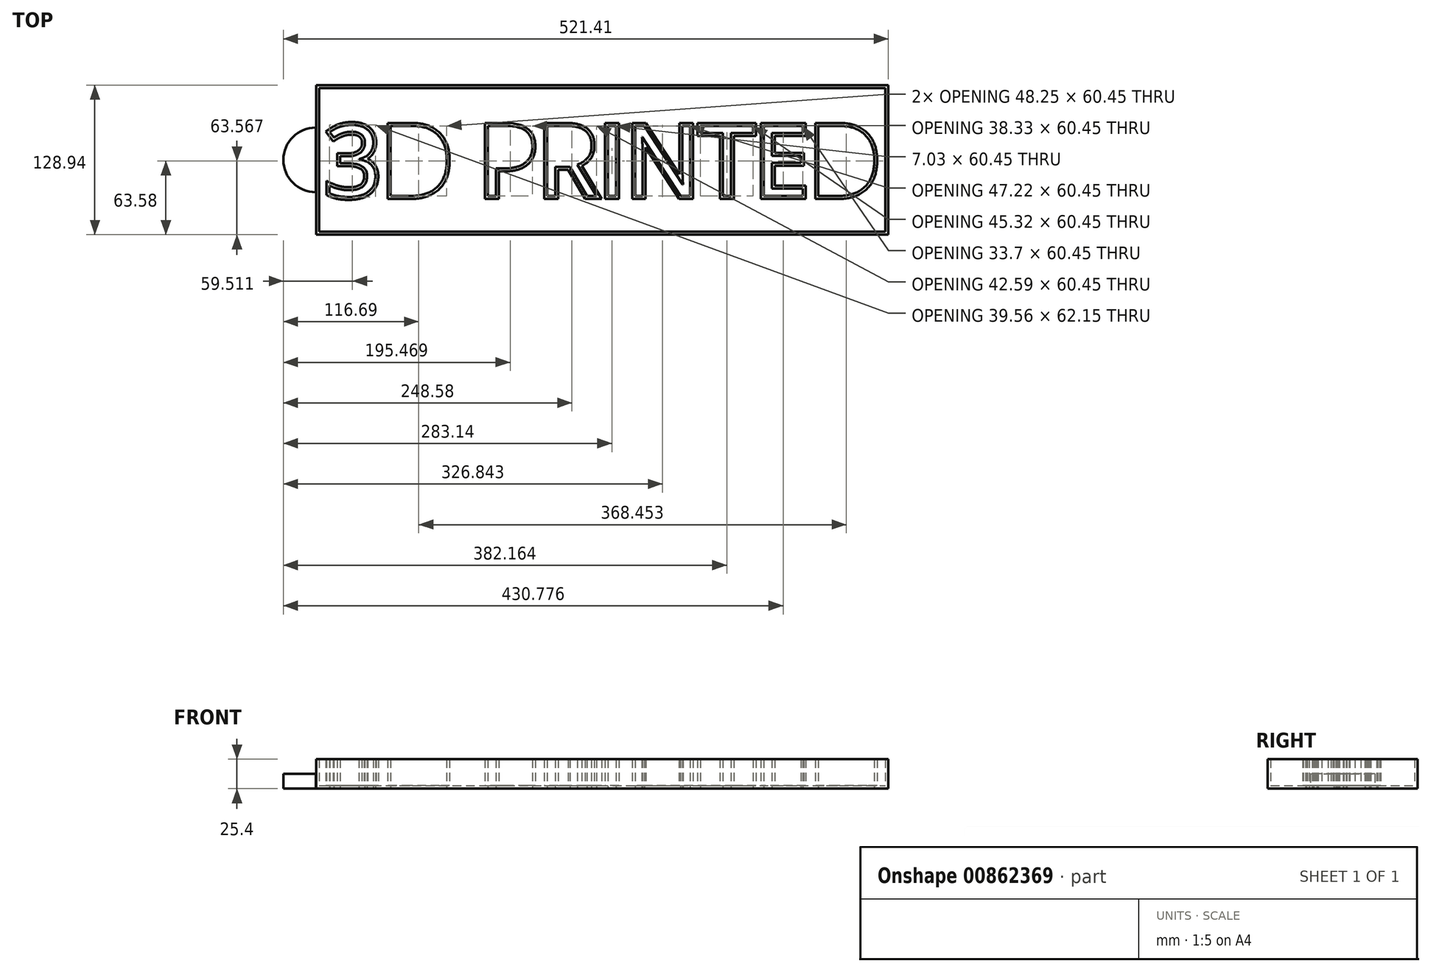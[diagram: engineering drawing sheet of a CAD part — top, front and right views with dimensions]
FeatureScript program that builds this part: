
annotation { "Feature Type Name" : "Feature", "Feature Type Description" : "" }
export const myFeature = defineFeature(function(context is Context, id is Id, definition is map)
    precondition{}
    {
        {
            var Q0;
            Q0=qCreatedBy(makeId("Top.planeOp"),FACE);
            var sketch = newSketch(context, id + "F0", { "sketchPlane" : qUnion([Q0])});
            skLineSegment(sketch, "E0.bottom", {"start": v(-246.53, -64.47) * mm, "end": v(246.53, -64.47) * mm});
            skLineSegment(sketch, "E0.top", {"start": v(-246.53, 64.47) * mm, "end": v(246.53, 64.47) * mm});
            skLineSegment(sketch, "E0.left", {"start": v(-246.53, -64.47) * mm, "end": v(-246.53, 64.47) * mm});
            skLineSegment(sketch, "E0.right", {"start": v(246.53, -64.47) * mm, "end": v(246.53, 64.47) * mm});
            skPoint(sketch, "E0.middle", {"position": v(0, 0) * mm});
            skText(sketch, "E1", { "text": "3D PRINTED\n", "fontName": "OpenSans-Regular.ttf"});
            const initialGuessF0  = {"E1": [-0.23904, -0.03113, 1, 0, 0.06097]};
            skSetInitialGuess(sketch, initialGuessF0);
            skSolve(sketch);
        }
        {
            var Q0;
            Q0 = qSketchRegion(id + "F0", true);
            var Q1;
            Q1=makeQuery(id+"F0.imprint","IMPRINT",FACE,{"disambiguationData":[TD([[makeQuery(id+"F0.imprint","IMPRINT",EDGE,{"derivedFrom":sQuery(id+"F0.wireOp",EDGE,"E0.bottom")}),1.0]])]});
            extrude(context, id + "F1", {"entities" : qUnion([Q0, Q1]), "depth" : 25.4 * mm, "offsetDistance" : 25.4 * mm});
        }
        {
            var Q0;
            Q0=makeQuery(id+"F1.opExtrude","CAP_FACE",FACE,{"disambiguationData":[OSD([sQuery(id+"F0.wireOp",EDGE,"E0.bottom"),sQuery(id+"F0.wireOp",EDGE,"E0.top"),sQuery(id+"F0.wireOp",EDGE,"E0.left"),sQuery(id+"F0.wireOp",EDGE,"E0.right")])],"isStart":false});
            shell(context, id + "F2", {"entities" : qUnion([Q0]), "thickness" : 2.54 * mm});
        }
        {
            var Q0;
            Q0=qCreatedBy(makeId("Top.planeOp"),FACE);
            var sketch = newSketch(context, id + "F3", { "sketchPlane" : qUnion([Q0])});
            skPoint(sketch, "E2.center.orphan", {"position": v(-247.02, 0) * mm});
            skArc(sketch, "E3", {"start": v(-247.02, 27.86) * mm, "mid": v(-274.88, 0) * mm, "end": v(-247.02, -27.86) * mm});
            skLineSegment(sketch, "E4", {"start": v(-247.02, 0) * mm, "end": v(-247.02, -39.54) * mm});
            skLineSegment(sketch, "E5", {"start": v(-247.02, -39.54) * mm, "end": v(-247.02, 41.5) * mm});
            skSolve(sketch);
        }
        {
            var Q0;
            Q0 = qSketchRegion(id + "F3", true);
            var Q1;
            {var subQ0=sQuery(id+"F3.wireOp",EDGE,"E3");Q1=makeQuery(id+"F3.imprint","IMPRINT",FACE,{"disambiguationData":[TD([[makeQuery(id+"F3.imprint","IMPRINT",EDGE,{"derivedFrom":subQ0}),1.0]])]});}
            extrude(context, id + "F4", {"entities" : qUnion([Q0, Q1]), "depth" : 12.7 * mm, "offsetDistance" : 25.4 * mm});
        }
        {
            var Q0;
            Q0=makeQuery(id+"F4.opExtrude","CAP_FACE",FACE,{"disambiguationData":[OSD([sQuery(id+"F3.wireOp",EDGE,"E3"),sQuery(id+"F3.wireOp",EDGE,"E5")])],"isStart":false});
            var sketch = newSketch(context, id + "F5", { "sketchPlane" : qUnion([Q0])});
            skCircle(sketch, "E6", {"center": v(-258.8, 0) * mm, "radius": 6.17 * mm});
            skSolve(sketch);
        }
        {
            var Q0;
            Q0 = qSketchRegion(id + "F5", true);
            extrude(context, id + "F6", {"entities" : qUnion([Q0]), "operationType" : NewBodyOperationType.ADD, "depth" : -12.7 * mm, "offsetDistance" : 25.4 * mm});
        }
        {
            var Q0;
            Q0 = qSketchRegion(id + "F5", true);
            extrude(context, id + "F7", {"entities" : qUnion([Q0]), "operationType" : NewBodyOperationType.ADD, "depth" : -12.7 * mm, "offsetDistance" : 25.4 * mm});
        }
    });
